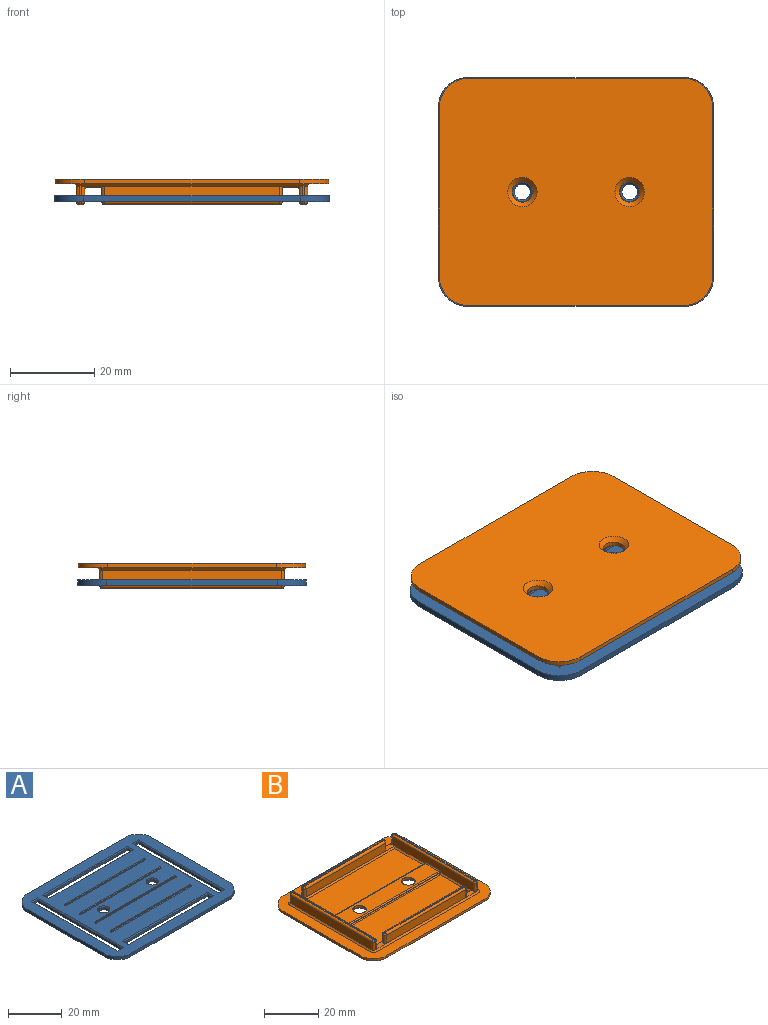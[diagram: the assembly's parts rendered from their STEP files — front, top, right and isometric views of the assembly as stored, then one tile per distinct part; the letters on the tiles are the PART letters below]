
ASSEMBLY  parts=2 mates=1
PART A: 146 faces, bbox 65.4x54.4x2 mm
  f0: plane 65.4x54.4mm, normal (0,0,1), area 2772.9mm2, adj f1,f2,f3,f4,f5,f6,f7,f21
  f1: plane 40.4x1.4mm, normal (-1,0,0), area 56.6mm2, adj f0,f2,f21,f27
  f2: cylinder r=7mm len=7mm, axis (0,0,1), area 15.4mm2, adj f0,f1,f3,f27
  f3: plane 51.4x1.4mm, normal (0,-1,0), area 72mm2, adj f0,f2,f4,f27
  f4: cylinder r=7mm len=7mm, axis (0,0,1), area 15.4mm2, adj f0,f3,f5,f27
  f5: plane 40.4x1.4mm, normal (1,0,0), area 56.6mm2, adj f0,f4,f6,f27
  f6: cylinder r=7mm len=7mm, axis (0,0,1), area 15.4mm2, adj f0,f5,f7,f27
  f7: plane 51.4x1.4mm, normal (0,1,0), area 72mm2, adj f0,f6,f21,f27
  f8: plane 44.4x1mm, normal (1,0,0), area 44.4mm2, adj f9,f22,f27,f138
  f9: plane 2.4x1mm, normal (0,-1,0), area 2.4mm2, adj f8,f10,f27,f136
  f10: plane 44.4x1mm, normal (-1,0,0), area 44.4mm2, adj f9,f22,f27,f137
  f11: plane 2.4x1mm, normal (-1,0,0), area 2.4mm2, adj f12,f23,f27,f132
  f12: plane 43.6x1mm, normal (0,1,0), area 43.6mm2, adj f11,f13,f27,f134
  f13: plane 2.4x1mm, normal (1,0,0), area 2.4mm2, adj f12,f23,f27,f135
  f14: plane 43.6x1mm, normal (0,-1,0), area 43.6mm2, adj f15,f24,f27,f130
  f15: plane 2.4x1mm, normal (-1,0,0), area 2.4mm2, adj f14,f16,f27,f131
  f16: plane 43.6x1mm, normal (0,1,0), area 43.6mm2, adj f15,f24,f27,f129
  f17: plane 2.4x1mm, normal (0,-1,0), area 2.4mm2, adj f18,f25,f27,f143
  f18: plane 44.4x1mm, normal (-1,0,0), area 44.4mm2, adj f17,f19,f27,f141
  f19: plane 2.4x1mm, normal (0,1,0), area 2.4mm2, adj f18,f25,f27,f140
  f20: cylinder r=1.88mm len=3.75mm, axis (0,0,1), area 11.8mm2, adj f27,f145
  f21: cylinder r=7mm len=7mm, axis (0,0,1), area 15.4mm2, adj f0,f1,f7,f27
  f22: plane 2.4x1mm, normal (0,1,0), area 2.4mm2, adj f8,f10,f27,f139
  f23: plane 43.6x1mm, normal (0,-1,0), area 43.6mm2, adj f11,f13,f27,f133
  f24: plane 2.4x1mm, normal (1,0,0), area 2.4mm2, adj f14,f16,f27,f128
  f25: plane 44.4x1mm, normal (1,0,0), area 44.4mm2, adj f17,f19,f27,f142
  f26: cylinder r=1.88mm len=3.75mm, axis (0,0,1), area 11.8mm2, adj f27,f144
  f27: plane 65.4x54.4mm, normal (0,0,-1), area 3071.2mm2, adj f1,f2,f3,f4,f5,f6,f7,f8
  f28: plane 41.6x0.2mm, normal (0,-1,0), area 8.3mm2, adj f48,f51,f55,f56
  f29: plane 0.2x0.01mm, normal (1,0,0), area 0mm2, adj f51,f52,f61,f62
  f30: plane 41.6x0.2mm, normal (0,1,0), area 8.3mm2, adj f53,f62,f63,f67
  f31: plane 0.2x0.01mm, normal (-1,0,0), area 0mm2, adj f54,f55,f63,f64
  f32: plane 41.6x0.01mm, normal (0,0,1), area 0.4mm2, adj f48,f52,f53,f54
  f33: plane 41.6x0.2mm, normal (0,-1,0), area 8.3mm2, adj f68,f71,f75,f76
  f34: plane 0.2x0.01mm, normal (1,0,0), area 0mm2, adj f71,f72,f81,f82
  f35: plane 41.6x0.2mm, normal (0,1,0), area 8.3mm2, adj f73,f82,f83,f87
  f36: plane 0.2x0.01mm, normal (-1,0,0), area 0mm2, adj f74,f75,f83,f84
  f37: plane 41.6x0.01mm, normal (0,0,1), area 0.4mm2, adj f68,f72,f73,f74
  f38: plane 41.6x0.2mm, normal (0,-1,0), area 8.3mm2, adj f91,f92,f101,f102
  f39: plane 0.2x0.01mm, normal (1,0,0), area 0mm2, adj f93,f102,f103,f107
  f40: plane 41.6x0.2mm, normal (0,1,0), area 8.3mm2, adj f94,f95,f103,f104
  f41: plane 0.2x0.01mm, normal (-1,0,0), area 0mm2, adj f88,f91,f95,f96
  f42: plane 41.6x0.01mm, normal (0,0,1), area 0.4mm2, adj f88,f92,f93,f94
  f43: plane 41.6x0.2mm, normal (0,-1,0), area 8.3mm2, adj f111,f112,f121,f122
  f44: plane 0.2x0.01mm, normal (1,0,0), area 0mm2, adj f108,f112,f113,f114
  f45: plane 41.6x0.2mm, normal (0,1,0), area 8.3mm2, adj f114,f115,f123,f124
  f46: plane 0.2x0.01mm, normal (-1,0,0), area 0mm2, adj f116,f121,f124,f127
  f47: plane 41.6x0.01mm, normal (0,0,1), area 0.4mm2, adj f108,f111,f115,f116
  f48: cylinder r=0.2mm len=41.6mm, axis (-1,0,0), area 13.1mm2, adj f28,f32,f49,f50
  f49: sphere r=0.2mm, area 0.1mm2, adj f48,f51,f52
  f50: sphere r=0.2mm, area 0.1mm2, adj f48,f54,f55
  f51: cylinder r=0.2mm len=0.2mm, axis (0,0,1), area 0.1mm2, adj f28,f29,f49,f57
  f52: cylinder r=0.2mm len=0.2mm, axis (0,-1,0), area 0mm2, adj f29,f32,f49,f58
  f53: cylinder r=0.2mm len=41.6mm, axis (1,0,0), area 13.1mm2, adj f30,f32,f58,f59
  f54: cylinder r=0.2mm len=0.2mm, axis (0,1,0), area 0mm2, adj f31,f32,f50,f59
  f55: cylinder r=0.2mm len=0.2mm, axis (0,0,-1), area 0.1mm2, adj f28,f31,f50,f60
  f56: cylinder r=0.2mm len=41.6mm, axis (1,0,0), area 13.1mm2, adj f0,f28,f57,f60
  f57: torus R=0.4mm, axis (0,0,1), area 0.1mm2, adj f0,f51,f56,f61
  f58: sphere r=0.2mm, area 0.1mm2, adj f52,f53,f62
  f59: sphere r=0.2mm, area 0.1mm2, adj f53,f54,f63
  f60: torus R=0.4mm, axis (0,0,1), area 0.1mm2, adj f0,f55,f56,f64
  f61: cylinder r=0.2mm len=0.2mm, axis (0,1,0), area 0mm2, adj f0,f29,f57,f65
  f62: cylinder r=0.2mm len=0.2mm, axis (0,0,-1), area 0.1mm2, adj f29,f30,f58,f65
  f63: cylinder r=0.2mm len=0.2mm, axis (0,0,1), area 0.1mm2, adj f30,f31,f59,f66
  f64: cylinder r=0.2mm len=0.2mm, axis (0,-1,0), area 0mm2, adj f0,f31,f60,f66
  f65: torus R=0.4mm, axis (0,0,1), area 0.1mm2, adj f0,f61,f62,f67
  f66: torus R=0.4mm, axis (0,0,1), area 0.1mm2, adj f0,f63,f64,f67
  f67: cylinder r=0.2mm len=41.6mm, axis (-1,0,0), area 13.1mm2, adj f0,f30,f65,f66
  f68: cylinder r=0.2mm len=41.6mm, axis (-1,0,0), area 13.1mm2, adj f33,f37,f69,f70
  f69: sphere r=0.2mm, area 0.1mm2, adj f68,f71,f72
  f70: sphere r=0.2mm, area 0.1mm2, adj f68,f74,f75
  f71: cylinder r=0.2mm len=0.2mm, axis (0,0,1), area 0.1mm2, adj f33,f34,f69,f77
  f72: cylinder r=0.2mm len=0.2mm, axis (0,-1,0), area 0mm2, adj f34,f37,f69,f78
  f73: cylinder r=0.2mm len=41.6mm, axis (1,0,0), area 13.1mm2, adj f35,f37,f78,f79
  f74: cylinder r=0.2mm len=0.2mm, axis (0,1,0), area 0mm2, adj f36,f37,f70,f79
  f75: cylinder r=0.2mm len=0.2mm, axis (0,0,-1), area 0.1mm2, adj f33,f36,f70,f80
  f76: cylinder r=0.2mm len=41.6mm, axis (1,0,0), area 13.1mm2, adj f0,f33,f77,f80
  f77: torus R=0.4mm, axis (0,0,1), area 0.1mm2, adj f0,f71,f76,f81
  f78: sphere r=0.2mm, area 0.1mm2, adj f72,f73,f82
  f79: sphere r=0.2mm, area 0.1mm2, adj f73,f74,f83
  f80: torus R=0.4mm, axis (0,0,1), area 0.1mm2, adj f0,f75,f76,f84
  f81: cylinder r=0.2mm len=0.2mm, axis (0,1,0), area 0mm2, adj f0,f34,f77,f85
  f82: cylinder r=0.2mm len=0.2mm, axis (0,0,-1), area 0.1mm2, adj f34,f35,f78,f85
  f83: cylinder r=0.2mm len=0.2mm, axis (0,0,1), area 0.1mm2, adj f35,f36,f79,f86
  f84: cylinder r=0.2mm len=0.2mm, axis (0,-1,0), area 0mm2, adj f0,f36,f80,f86
  f85: torus R=0.4mm, axis (0,0,1), area 0.1mm2, adj f0,f81,f82,f87
  f86: torus R=0.4mm, axis (0,0,1), area 0.1mm2, adj f0,f83,f84,f87
  f87: cylinder r=0.2mm len=41.6mm, axis (-1,0,0), area 13.1mm2, adj f0,f35,f85,f86
  f88: cylinder r=0.2mm len=0.2mm, axis (0,1,0), area 0mm2, adj f41,f42,f89,f90
  f89: sphere r=0.2mm, area 0.1mm2, adj f88,f91,f92
  f90: sphere r=0.2mm, area 0.1mm2, adj f88,f94,f95
  f91: cylinder r=0.2mm len=0.2mm, axis (0,0,-1), area 0.1mm2, adj f38,f41,f89,f97
  f92: cylinder r=0.2mm len=41.6mm, axis (-1,0,0), area 13.1mm2, adj f38,f42,f89,f98
  f93: cylinder r=0.2mm len=0.2mm, axis (0,-1,0), area 0mm2, adj f39,f42,f98,f99
  f94: cylinder r=0.2mm len=41.6mm, axis (1,0,0), area 13.1mm2, adj f40,f42,f90,f99
  f95: cylinder r=0.2mm len=0.2mm, axis (0,0,1), area 0.1mm2, adj f40,f41,f90,f100
  f96: cylinder r=0.2mm len=0.2mm, axis (0,-1,0), area 0mm2, adj f0,f41,f97,f100
  f97: torus R=0.4mm, axis (0,0,1), area 0.1mm2, adj f0,f91,f96,f101
  f98: sphere r=0.2mm, area 0.1mm2, adj f92,f93,f102
  f99: sphere r=0.2mm, area 0.1mm2, adj f93,f94,f103
  f100: torus R=0.4mm, axis (0,0,1), area 0.1mm2, adj f0,f95,f96,f104
  f101: cylinder r=0.2mm len=41.6mm, axis (1,0,0), area 13.1mm2, adj f0,f38,f97,f105
  f102: cylinder r=0.2mm len=0.2mm, axis (0,0,1), area 0.1mm2, adj f38,f39,f98,f105
  f103: cylinder r=0.2mm len=0.2mm, axis (0,0,-1), area 0.1mm2, adj f39,f40,f99,f106
  f104: cylinder r=0.2mm len=41.6mm, axis (-1,0,0), area 13.1mm2, adj f0,f40,f100,f106
  f105: torus R=0.4mm, axis (0,0,1), area 0.1mm2, adj f0,f101,f102,f107
  f106: torus R=0.4mm, axis (0,0,1), area 0.1mm2, adj f0,f103,f104,f107
  f107: cylinder r=0.2mm len=0.2mm, axis (0,1,0), area 0mm2, adj f0,f39,f105,f106
  f108: cylinder r=0.2mm len=0.2mm, axis (0,-1,0), area 0mm2, adj f44,f47,f109,f110
  f109: sphere r=0.2mm, area 0.1mm2, adj f108,f111,f112
  f110: sphere r=0.2mm, area 0.1mm2, adj f108,f114,f115
  f111: cylinder r=0.2mm len=41.6mm, axis (-1,0,0), area 13.1mm2, adj f43,f47,f109,f117
  f112: cylinder r=0.2mm len=0.2mm, axis (0,0,1), area 0.1mm2, adj f43,f44,f109,f118
  f113: cylinder r=0.2mm len=0.2mm, axis (0,1,0), area 0mm2, adj f0,f44,f118,f119
  f114: cylinder r=0.2mm len=0.2mm, axis (0,0,-1), area 0.1mm2, adj f44,f45,f110,f119
  f115: cylinder r=0.2mm len=41.6mm, axis (1,0,0), area 13.1mm2, adj f45,f47,f110,f120
  f116: cylinder r=0.2mm len=0.2mm, axis (0,1,0), area 0mm2, adj f46,f47,f117,f120
  f117: sphere r=0.2mm, area 0.1mm2, adj f111,f116,f121
  f118: torus R=0.4mm, axis (0,0,1), area 0.1mm2, adj f0,f112,f113,f122
  f119: torus R=0.4mm, axis (0,0,1), area 0.1mm2, adj f0,f113,f114,f123
  f120: sphere r=0.2mm, area 0.1mm2, adj f115,f116,f124
  f121: cylinder r=0.2mm len=0.2mm, axis (0,0,-1), area 0.1mm2, adj f43,f46,f117,f125
  f122: cylinder r=0.2mm len=41.6mm, axis (1,0,0), area 13.1mm2, adj f0,f43,f118,f125
  f123: cylinder r=0.2mm len=41.6mm, axis (-1,0,0), area 13.1mm2, adj f0,f45,f119,f126
  f124: cylinder r=0.2mm len=0.2mm, axis (0,0,1), area 0.1mm2, adj f45,f46,f120,f126
  f125: torus R=0.4mm, axis (0,0,1), area 0.1mm2, adj f0,f121,f122,f127
  f126: torus R=0.4mm, axis (0,0,1), area 0.1mm2, adj f0,f123,f124,f127
  f127: cylinder r=0.2mm len=0.2mm, axis (0,-1,0), area 0mm2, adj f0,f46,f125,f126
  f128: plane 3.2x0.4mm, normal (0.71,0,0.71), area 1.6mm2, adj f0,f24,f129,f130
  f129: plane 44.4x0.4mm, normal (0,0.71,0.71), area 24.9mm2, adj f0,f16,f128,f131
  f130: plane 44.4x0.4mm, normal (0,-0.71,0.71), area 24.9mm2, adj f0,f14,f128,f131
  f131: plane 3.2x0.4mm, normal (-0.71,0,0.71), area 1.6mm2, adj f0,f15,f129,f130
  f132: plane 3.2x0.4mm, normal (-0.71,0,0.71), area 1.6mm2, adj f0,f11,f133,f134
  f133: plane 44.4x0.4mm, normal (0,-0.71,0.71), area 24.9mm2, adj f0,f23,f132,f135
  f134: plane 44.4x0.4mm, normal (0,0.71,0.71), area 24.9mm2, adj f0,f12,f132,f135
  f135: plane 3.2x0.4mm, normal (0.71,0,0.71), area 1.6mm2, adj f0,f13,f133,f134
  f136: plane 3.2x0.4mm, normal (0,-0.71,0.71), area 1.6mm2, adj f0,f9,f137,f138
  f137: plane 45.2x0.4mm, normal (-0.71,0,0.71), area 25.3mm2, adj f0,f10,f136,f139
  f138: plane 45.2x0.4mm, normal (0.71,0,0.71), area 25.3mm2, adj f0,f8,f136,f139
  f139: plane 3.2x0.4mm, normal (0,0.71,0.71), area 1.6mm2, adj f0,f22,f137,f138
  f140: plane 3.2x0.4mm, normal (0,0.71,0.71), area 1.6mm2, adj f0,f19,f141,f142
  f141: plane 45.2x0.4mm, normal (-0.71,0,0.71), area 25.3mm2, adj f0,f18,f140,f143
  f142: plane 45.2x0.4mm, normal (0.71,0,0.71), area 25.3mm2, adj f0,f25,f140,f143
  f143: plane 3.2x0.4mm, normal (0,-0.71,0.71), area 1.6mm2, adj f0,f17,f141,f142
  f144: cone r=1.88mm half-angle=45deg, axis (0,0,1), area 7.4mm2, adj f0,f26
  f145: cone r=1.88mm half-angle=45deg, axis (0,0,1), area 7.4mm2, adj f0,f20
PART B: 119 faces, bbox 65x54x6 mm
  f0: plane 42.4x3.6mm, normal (1,0,0), area 145.9mm2, adj f4,f33,f35,f38,f43,f44,f96,f107
  f1: plane 42.4x3.6mm, normal (-1,0,0), area 145.9mm2, adj f3,f31,f37,f79,f83,f85,f95,f111
  f2: plane 49.8x15mm, normal (0,0,1), area 747mm2, adj f95,f96,f97,f106
  f3: plane 15.99x0.6mm, normal (-0.71,0,0.71), area 13.2mm2, adj f1,f15,f94,f117,f118
  f4: plane 15.99x0.6mm, normal (0.71,0,0.71), area 13.2mm2, adj f0,f15,f94,f115,f117
  f5: plane 3.6x0.4mm, normal (0,1,0), area 1.4mm2, adj f76,f82,f85,f86
  f6: plane 41.4x3.6mm, normal (0,1,0), area 149mm2, adj f67,f70,f73,f86
  f7: plane 3.6x0.4mm, normal (0,-1,0), area 1.4mm2, adj f44,f45,f49,f93
  f8: plane 41.4x3.6mm, normal (0,-1,0), area 149mm2, adj f56,f57,f61,f93
  f9: plane 41.4x3.6mm, normal (0,1,0), area 149mm2, adj f50,f51,f52,f94
  f10: plane 41.4x3.6mm, normal (0,-1,0), area 149mm2, adj f62,f63,f64,f97
  f11: plane 42.4x0.4mm, normal (0,0,1), area 17mm2, adj f77,f78,f82,f83
  f12: plane 42.4x0.4mm, normal (0,0,1), area 17mm2, adj f40,f43,f46,f49
  f13: plane 41.4x0.4mm, normal (0,0,1), area 16.6mm2, adj f63,f68,f69,f73
  f14: plane 3.6x0.4mm, normal (0,-1,0), area 1.4mm2, adj f74,f78,f79,f93
  f15: plane 49.8x15mm, normal (0,0,1), area 747mm2, adj f3,f4,f94,f117
  f16: plane 65x54mm, normal (0,0,1), area 929.4mm2, adj f17,f18,f19,f20,f21,f22,f23,f24
  f17: plane 40x1mm, normal (-1,0,0), area 40mm2, adj f16,f18,f24,f25
  f18: cylinder r=7mm len=7mm, axis (0,0,1), area 11mm2, adj f16,f17,f19,f25
  f19: plane 51x1mm, normal (0,-1,0), area 51mm2, adj f16,f18,f20,f25
  f20: cylinder r=7mm len=7mm, axis (0,0,1), area 11mm2, adj f16,f19,f21,f25
  f21: plane 40x1mm, normal (1,0,0), area 40mm2, adj f16,f20,f22,f25
  f22: cylinder r=7mm len=7mm, axis (0,0,1), area 11mm2, adj f16,f21,f23,f25
  f23: plane 51x1mm, normal (0,1,0), area 51mm2, adj f16,f22,f24,f25
  f24: cylinder r=7mm len=7mm, axis (0,0,1), area 11mm2, adj f16,f17,f23,f25
  f25: plane 65x54mm, normal (0,0,-1), area 3391mm2, adj f17,f18,f19,f20,f21,f22,f23,f24
  f26: plane 42.4x3.6mm, normal (-1,0,0), area 152.6mm2, adj f39,f45,f46,f90
  f27: plane 42.4x3.6mm, normal (1,0,0), area 152.6mm2, adj f74,f76,f77,f89
  f28: plane 3.6x0.4mm, normal (0,1,0), area 1.4mm2, adj f38,f39,f40,f86
  f29: plane 41.4x0.4mm, normal (0,0,1), area 16.6mm2, adj f52,f55,f58,f61
  f30: plane 3.6x0.4mm, normal (1,0,0), area 1.4mm2, adj f31,f62,f67,f68
  f31: plane 5.6x2mm, normal (0,0,1), area 8.4mm2, adj f1,f30,f62,f67,f85,f86,f97
  f32: plane 3.6x0.4mm, normal (-1,0,0), area 1.4mm2, adj f33,f64,f69,f70
  f33: plane 5.6x2mm, normal (0,0,1), area 8.4mm2, adj f0,f32,f38,f64,f70,f86,f97
  f34: plane 3.6x0.4mm, normal (-1,0,0), area 1.4mm2, adj f35,f51,f57,f58
  f35: plane 5.6x2mm, normal (0,0,1), area 8.4mm2, adj f0,f34,f44,f51,f57,f93,f94
  f36: plane 3.6x0.4mm, normal (1,0,0), area 1.4mm2, adj f37,f50,f55,f56
  f37: plane 5.6x2mm, normal (0,0,1), area 8.4mm2, adj f1,f36,f50,f56,f79,f93,f94
  f38: cylinder r=0.8mm len=3.6mm, axis (0,0,1), area 4.5mm2, adj f0,f28,f33,f41
  f39: cylinder r=0.8mm len=3.6mm, axis (0,0,1), area 4.5mm2, adj f26,f28,f42,f88
  f40: cylinder r=0.8mm len=0.8mm, axis (1,0,0), area 0.5mm2, adj f12,f28,f41,f42
  f41: sphere r=0.8mm, area 1mm2, adj f38,f40,f43
  f42: sphere r=0.8mm, area 1mm2, adj f39,f40,f46
  f43: cylinder r=0.8mm len=42.4mm, axis (0,-1,0), area 53.3mm2, adj f0,f12,f41,f47
  f44: cylinder r=0.8mm len=3.6mm, axis (0,0,-1), area 4.5mm2, adj f0,f7,f35,f47
  f45: cylinder r=0.8mm len=3.6mm, axis (0,0,-1), area 4.5mm2, adj f7,f26,f48,f92
  f46: cylinder r=0.8mm len=42.4mm, axis (0,1,0), area 53.3mm2, adj f12,f26,f42,f48
  f47: sphere r=0.8mm, area 1mm2, adj f43,f44,f49
  f48: sphere r=0.8mm, area 1mm2, adj f45,f46,f49
  f49: cylinder r=0.8mm len=0.8mm, axis (-1,0,0), area 0.5mm2, adj f7,f12,f47,f48
  f50: cylinder r=0.8mm len=3.6mm, axis (0,0,1), area 4.5mm2, adj f9,f36,f37,f53
  f51: cylinder r=0.8mm len=3.6mm, axis (0,0,-1), area 4.5mm2, adj f9,f34,f35,f54
  f52: cylinder r=0.8mm len=41.4mm, axis (1,0,0), area 52mm2, adj f9,f29,f53,f54
  f53: sphere r=0.8mm, area 1mm2, adj f50,f52,f55
  f54: sphere r=0.8mm, area 1mm2, adj f51,f52,f58
  f55: cylinder r=0.8mm len=0.8mm, axis (0,1,0), area 0.5mm2, adj f29,f36,f53,f59
  f56: cylinder r=0.8mm len=3.6mm, axis (0,0,-1), area 4.5mm2, adj f8,f36,f37,f59
  f57: cylinder r=0.8mm len=3.6mm, axis (0,0,1), area 4.5mm2, adj f8,f34,f35,f60
  f58: cylinder r=0.8mm len=0.8mm, axis (0,-1,0), area 0.5mm2, adj f29,f34,f54,f60
  f59: sphere r=0.8mm, area 1mm2, adj f55,f56,f61
  f60: sphere r=0.8mm, area 1mm2, adj f57,f58,f61
  f61: cylinder r=0.8mm len=41.4mm, axis (-1,0,0), area 52mm2, adj f8,f29,f59,f60
  f62: cylinder r=0.8mm len=3.6mm, axis (0,0,1), area 4.5mm2, adj f10,f30,f31,f65
  f63: cylinder r=0.8mm len=41.4mm, axis (-1,0,0), area 52mm2, adj f10,f13,f65,f66
  f64: cylinder r=0.8mm len=3.6mm, axis (0,0,-1), area 4.5mm2, adj f10,f32,f33,f66
  f65: sphere r=0.8mm, area 1mm2, adj f62,f63,f68
  f66: sphere r=0.8mm, area 1mm2, adj f63,f64,f69
  f67: cylinder r=0.8mm len=3.6mm, axis (0,0,-1), area 4.5mm2, adj f6,f30,f31,f71
  f68: cylinder r=0.8mm len=0.8mm, axis (0,1,0), area 0.5mm2, adj f13,f30,f65,f71
  f69: cylinder r=0.8mm len=0.8mm, axis (0,-1,0), area 0.5mm2, adj f13,f32,f66,f72
  f70: cylinder r=0.8mm len=3.6mm, axis (0,0,1), area 4.5mm2, adj f6,f32,f33,f72
  f71: sphere r=0.8mm, area 1mm2, adj f67,f68,f73
  f72: sphere r=0.8mm, area 1mm2, adj f69,f70,f73
  f73: cylinder r=0.8mm len=41.4mm, axis (1,0,0), area 52mm2, adj f6,f13,f71,f72
  f74: cylinder r=0.8mm len=3.6mm, axis (0,0,1), area 4.5mm2, adj f14,f27,f75,f91
  f75: sphere r=0.8mm, area 1mm2, adj f74,f77,f78
  f76: cylinder r=0.8mm len=3.6mm, axis (0,0,-1), area 4.5mm2, adj f5,f27,f80,f87
  f77: cylinder r=0.8mm len=42.4mm, axis (0,-1,0), area 53.3mm2, adj f11,f27,f75,f80
  f78: cylinder r=0.8mm len=0.8mm, axis (-1,0,0), area 0.5mm2, adj f11,f14,f75,f81
  f79: cylinder r=0.8mm len=3.6mm, axis (0,0,1), area 4.5mm2, adj f1,f14,f37,f81
  f80: sphere r=0.8mm, area 1mm2, adj f76,f77,f82
  f81: sphere r=0.8mm, area 1mm2, adj f78,f79,f83
  f82: cylinder r=0.8mm len=0.8mm, axis (1,0,0), area 0.5mm2, adj f5,f11,f80,f84
  f83: cylinder r=0.8mm len=42.4mm, axis (0,1,0), area 53.3mm2, adj f1,f11,f81,f84
  f84: sphere r=0.8mm, area 1mm2, adj f82,f83,f85
  f85: cylinder r=0.8mm len=3.6mm, axis (0,0,-1), area 4.5mm2, adj f1,f5,f31,f84
  f86: plane 53.4x0.6mm, normal (0,0.71,0.71), area 45.3mm2, adj f5,f6,f16,f28,f31,f33,f87,f88
  f87: cone r=1.4mm half-angle=45deg, axis (0,0,-1), area 1.5mm2, adj f16,f76,f86,f89
  f88: cone r=1.4mm half-angle=45deg, axis (0,0,-1), area 1.5mm2, adj f16,f39,f86,f90
  f89: plane 42.4x0.6mm, normal (0.71,0,0.71), area 36mm2, adj f16,f27,f87,f91
  f90: plane 42.4x0.6mm, normal (-0.71,0,0.71), area 36mm2, adj f16,f26,f88,f92
  f91: cone r=1.4mm half-angle=45deg, axis (0,0,-1), area 1.5mm2, adj f16,f74,f89,f93
  f92: cone r=1.4mm half-angle=45deg, axis (0,0,-1), area 1.5mm2, adj f16,f45,f90,f93
  f93: plane 53.4x0.6mm, normal (0,-0.71,0.71), area 45.3mm2, adj f7,f8,f14,f16,f35,f37,f91,f92
  f94: plane 51x0.6mm, normal (0,0.71,0.71), area 42.8mm2, adj f3,f4,f9,f15,f35,f37
  f95: plane 15.99x0.6mm, normal (-0.71,0,0.71), area 13.2mm2, adj f1,f2,f97,f106,f109
  f96: plane 15.99x0.6mm, normal (0.71,0,0.71), area 13.2mm2, adj f0,f2,f97,f105,f106
  f97: plane 51x0.6mm, normal (0,-0.71,0.71), area 42.8mm2, adj f2,f10,f31,f33,f95,f96
  f98: cone r=3.5mm half-angle=45deg, axis (0,0,-1), area 26.7mm2, adj f25,f103
  f99: cone r=3.5mm half-angle=45deg, axis (0,0,-1), area 26.7mm2, adj f25,f102
  f100: plane 50.2x0.2mm, normal (0,-1,0), area 10mm2, adj f113,f115,f117,f118
  f101: plane 50.2x0.2mm, normal (0,1,0), area 10mm2, adj f105,f106,f108,f109
  f102: cylinder r=2.5mm len=5mm, axis (0,0,-1), area 15.7mm2, adj f99,f104
  f103: cylinder r=2.5mm len=5mm, axis (0,0,-1), area 15.7mm2, adj f98,f104
  f104: plane 50.2x7.2mm, normal (0,0,1), area 322.2mm2, adj f102,f103,f108,f110,f113,f114
  f105: cylinder r=0.4mm len=0.4mm, axis (0,0,-1), area 0.1mm2, adj f96,f101,f106,f107
  f106: cylinder r=0.4mm len=50.4mm, axis (-1,0,0), area 31.5mm2, adj f2,f95,f96,f101,f105,f109
  f107: torus R=0.8mm, axis (-1,0,0), area 0.5mm2, adj f0,f105,f108,f110
  f108: cylinder r=0.4mm len=50.2mm, axis (1,0,0), area 31.5mm2, adj f101,f104,f107,f111
  f109: cylinder r=0.4mm len=0.4mm, axis (0,0,1), area 0.1mm2, adj f95,f101,f106,f111
  f110: cylinder r=0.4mm len=7.2mm, axis (0,1,0), area 4.5mm2, adj f0,f104,f107,f112
  f111: torus R=0.8mm, axis (-1,0,0), area 0.5mm2, adj f1,f108,f109,f114
  f112: torus R=0.8mm, axis (-1,0,0), area 0.5mm2, adj f0,f110,f113,f115
  f113: cylinder r=0.4mm len=50.2mm, axis (-1,0,0), area 31.5mm2, adj f100,f104,f112,f116
  f114: cylinder r=0.4mm len=7.2mm, axis (0,-1,0), area 4.5mm2, adj f1,f104,f111,f116
  f115: cylinder r=0.4mm len=0.4mm, axis (0,0,1), area 0.1mm2, adj f4,f100,f112,f117
  f116: torus R=0.8mm, axis (-1,0,0), area 0.5mm2, adj f1,f113,f114,f118
  f117: cylinder r=0.4mm len=50.4mm, axis (1,0,0), area 31.5mm2, adj f3,f4,f15,f100,f115,f118
  f118: cylinder r=0.4mm len=0.4mm, axis (0,0,-1), area 0.1mm2, adj f3,f100,f116,f117
PLACE A rot(axis=(0,0,1),180deg) t=(-77.81,-6.74,14.03)mm
PLACE B rot(axis=(0,-1,0),180deg) t=(-77.81,-6.74,16.89)mm
MATE slider A.f0 <-> B.f104  axis (0,0,1) through (-77.81,-6.74,14.03)mm
